# Revit family: Taza Carlton
name_source: partatom
category: Aparatos sanitarios
units: mm (PartAtom-declared; Revit-internal decimal feet)

## family parameters
Compartido = Sí
Corte con vacíos al cargar = No
Cota de conector redondo = Diámetro de uso
Número OmniClass = 23.45.00.00
Punto de cálculo de habitación = Sí
Se basa en plano de trabajo = No
Siempre vertical = Sí
Tipo de pieza = Normal
Título OmniClass = Sanitary, Laundry, and Cleaning Equipment

## types (1)
- BELA MONOMANDO PARA LAVAMANOS CROMO
    Conexión AC = Sí
    Conexión AF = Sí
    Conexión de residuos = Sí
    Conexión de ventilación = Sí
    Fabricante = EDESA Ecuador
    Imagen de tipo = <Ninguno>
    Modelo = 00
    _ALT_Basamento = 0.4 m
    _ALT_Eje instalación = 0.6 m
    _EDESA_ Alto en cm = 0
    _EDESA_ Ancho en cm = 0
    _EDESA_ Certificación = 0
    _EDESA_ Color = 0 m
    _EDESA_ Consumo/capacidad de agua en L = 0
    _EDESA_ Descripción = 0
    _EDESA_ Distancia de instalación en cm (muro terminado) = 0
    _EDESA_ Marca = 0
    _EDESA_ Nombre = 0
    _EDESA_ Peso en kg = 0
    _EDESA_ Productos incluídos = 0
    _EDESA_ Productos necesarios para instalación = 0
    _EDESA_ Profundidad en cm = 0
    _EDESA_ Página web = 0
    _EDESA_ Sku/código = 0 m
    _EDESA_ Tipo de Aro = 0
    _EDESA_ Tipo de instalación = 0
    _EDESA_ Tolerancia dimensional = 0 m
